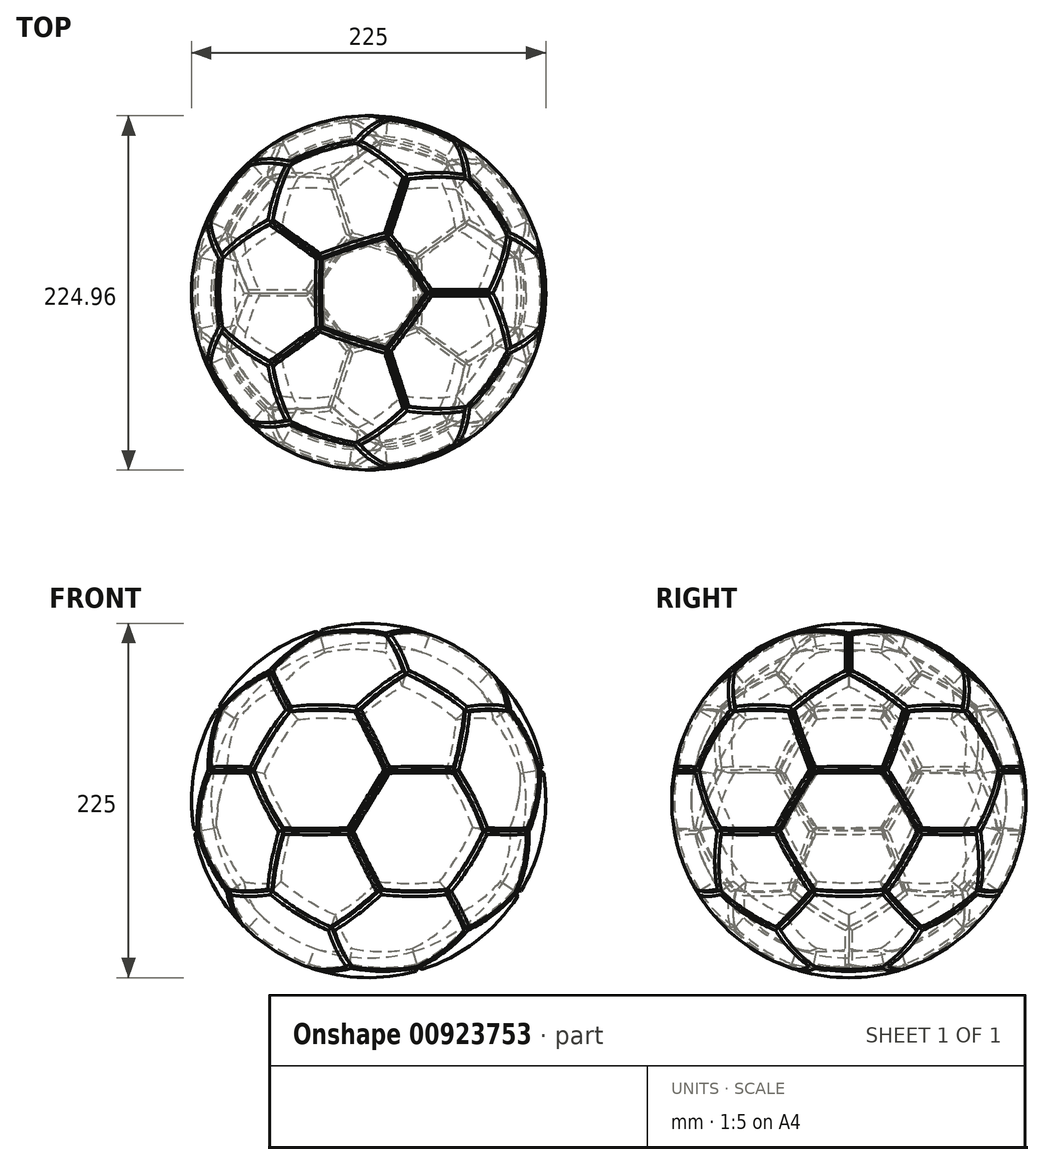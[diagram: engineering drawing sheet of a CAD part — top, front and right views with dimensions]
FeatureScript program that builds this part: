
annotation { "Feature Type Name" : "Feature", "Feature Type Description" : "" }
export const myFeature = defineFeature(function(context is Context, id is Id, definition is map)
    precondition{}
    {
        {
            var Q0;
            Q0=qCreatedBy(makeId("Top.planeOp"),FACE);
            var sketch = newSketch(context, id + "F0", { "sketchPlane" : qUnion([Q0])});
            skLineSegment(sketch, "E0.0", {"start": v(-13.14, 40.45) * mm, "end": v(34.4, 25) * mm});
            skLineSegment(sketch, "E0.1", {"start": v(34.4, 25) * mm, "end": v(34.4, -25) * mm});
            skLineSegment(sketch, "E0.2", {"start": v(34.4, -25) * mm, "end": v(-13.14, -40.45) * mm});
            skLineSegment(sketch, "E0.3", {"start": v(-13.14, -40.45) * mm, "end": v(-42.53, 0) * mm});
            skLineSegment(sketch, "E0.4", {"start": v(-42.53, 0) * mm, "end": v(-13.14, 40.45) * mm});
            skLineSegment(sketch, "E1", {"start": v(34.4, -25) * mm, "end": v(34.4, -50) * mm, "construction": true});
            skLineSegment(sketch, "E2", {"start": v(77.71, -50) * mm, "end": v(34.4, -50) * mm, "construction": true});
            skLineSegment(sketch, "E3", {"start": v(34.4, -25) * mm, "end": v(-27.84, 20.23) * mm, "construction": true});
            skLineSegment(sketch, "E4.MirrorCS", {"start": v(34.4, -25) * mm, "end": v(58.19, -17.27) * mm, "construction": true});
            skLineSegment(sketch, "E5.MirrorCS", {"start": v(71.57, -58.46) * mm, "end": v(58.19, -17.27) * mm, "construction": true});
            skSolve(sketch);
        }
        {
            var Q0;
            Q0=sQuery(id+"F0.wireOp",VERTEX,"E1.end");
            var Q1;
            Q1=sQuery(id+"F0.wireOp",EDGE,"E1");
            cPlane(context, id + "F1", {"entities" : qUnion([Q0, Q1]), "cplaneType" : CPlaneType.LINE_POINT, "offset" : 25 * mm, "width" : 150 * mm, "height" : 150 * mm});
        }
        {
            var Q0;
            Q0=qCreatedBy(id+"F1.planeOp",FACE);
            var sketch = newSketch(context, id + "F2", { "sketchPlane" : qUnion([Q0])});
            skCircle(sketch, "E6", {"center": v(34.4, 0) * mm, "radius": 43.3 * mm});
            skSolve(sketch);
        }
        {
            var Q0;
            Q0=sQuery(id+"F0.wireOp",VERTEX,"E4.MirrorCS.end");
            var Q1;
            Q1=sQuery(id+"F0.wireOp",EDGE,"E4.MirrorCS");
            cPlane(context, id + "F3", {"entities" : qUnion([Q0, Q1]), "cplaneType" : CPlaneType.LINE_POINT, "offset" : 25 * mm, "width" : 150 * mm, "height" : 150 * mm});
        }
        {
            var Q0;
            Q0=qCreatedBy(id+"F3.planeOp",FACE);
            var sketch = newSketch(context, id + "F4", { "sketchPlane" : qUnion([Q0])});
            skCircle(sketch, "E7", {"center": v(-34.4, 0) * mm, "radius": 43.3 * mm});
            skSolve(sketch);
        }
        {
            var Q0;
            Q0=makeQuery(id+"F2.imprint","IMPRINT",FACE,{"disambiguationData":[TD([[makeQuery(id+"F2.imprint","IMPRINT",EDGE,{"derivedFrom":sQuery(id+"F2.wireOp",EDGE,"E6")}),1.0]])]});
            extrude(context, id + "F5", {"entities" : qUnion([Q0]), "depth" : 25 * mm, "offsetDistance" : 25 * mm});
        }
        {
            var Q0;
            Q0=makeQuery(id+"F4.imprint","IMPRINT",FACE,{"disambiguationData":[TD([[makeQuery(id+"F4.imprint","IMPRINT",EDGE,{"derivedFrom":sQuery(id+"F4.wireOp",EDGE,"E7")}),1.0]])]});
            extrude(context, id + "F6", {"entities" : qUnion([Q0]), "depth" : 25 * mm, "offsetDistance" : 25 * mm});
        }
        {
            var Q0;
            Q0=makeQuery(id+"F5.opExtrude","SWEPT_BODY",BODY,{"disambiguationData":[OSD([sQuery(id+"F2.wireOp",EDGE,"E6")])]});
            var Q1;
            Q1=makeQuery(id+"F6.opExtrude","SWEPT_BODY",BODY,{"disambiguationData":[OSD([sQuery(id+"F4.wireOp",EDGE,"E7")])]});
            booleanBodies(context, id + "F7", {"operationType" : BooleanOperationType.INTERSECTION, "tools" : qUnion([Q0, Q1])});
        }
        {
            var Q0;
            Q0=sQuery(id+"F0.wireOp",VERTEX,"E0.0.end");
            var Q1;
            Q1=sQuery(id+"F0.wireOp",VERTEX,"E0.1.end");
            var Q2;
            {var subQ0=sQuery(id+"F4.wireOp",EDGE,"E7");var subQ1=sQuery(id+"F2.wireOp",EDGE,"E6");Q2=makeQuery(id+"F7.opBoolean","INTERSECT",VERTEX,{"disambiguationData":[OD(1.0)],"derivedFrom":[makeQuery(id+"F5.opExtrude","SWEPT_FACE",FACE,{"disambiguationData":[OSD([subQ1])]}),makeQuery(id+"F5.opExtrude","CAP_FACE",FACE,{"disambiguationData":[OSD([subQ1])],"isStart":true}),makeQuery(id+"F6.opExtrude","SWEPT_FACE",FACE,{"disambiguationData":[OSD([subQ0])]}),makeQuery(id+"F6.opExtrude","CAP_FACE",FACE,{"disambiguationData":[OSD([subQ0])],"isStart":true})]});}
            cPlane(context, id + "F8", {"entities" : qUnion([Q0, Q1, Q2]), "cplaneType" : CPlaneType.THREE_POINT, "offset" : 25 * mm, "width" : 150 * mm, "height" : 150 * mm});
        }
        {
            var Q0;
            Q0=qCreatedBy(id+"F8.planeOp",FACE);
            var sketch = newSketch(context, id + "F9", { "sketchPlane" : qUnion([Q0])});
            skLineSegment(sketch, "E8.0", {"start": v(113.95, 25) * mm, "end": v(113.95, -25) * mm});
            skLineSegment(sketch, "E8.1", {"start": v(113.95, -25) * mm, "end": v(70.64, -50) * mm});
            skLineSegment(sketch, "E8.2", {"start": v(70.64, -50) * mm, "end": v(27.34, -25) * mm});
            skLineSegment(sketch, "E8.3", {"start": v(27.34, -25) * mm, "end": v(27.34, 25) * mm});
            skLineSegment(sketch, "E8.4", {"start": v(27.34, 25) * mm, "end": v(70.64, 50) * mm});
            skLineSegment(sketch, "E8.5", {"start": v(70.64, 50) * mm, "end": v(113.95, 25) * mm});
            skLineSegment(sketch, "E9", {"start": v(70.64, 0) * mm, "end": v(27.34, -25) * mm, "construction": true});
            skSolve(sketch);
        }
        {
            var Q0;
            Q0=qCreatedBy(makeId("Front.planeOp"),FACE);
            var sketch = newSketch(context, id + "F10", { "sketchPlane" : qUnion([Q0])});
            skLineSegment(sketch, "E10", {"start": v(0, 0) * mm, "end": v(0, 116.37) * mm, "construction": true});
            skLineSegment(sketch, "E11", {"start": v(68.82, 26.29) * mm, "end": v(0, 116.37) * mm, "construction": true});
            skSolve(sketch);
        }
        {
            var Q0;
            Q0=makeQuery(id+"F0.imprint","IMPRINT",FACE,{"disambiguationData":[TD([[makeQuery(id+"F0.imprint","IMPRINT",EDGE,{"derivedFrom":sQuery(id+"F0.wireOp",EDGE,"E0.0")}),-1.0]])]});
            var Q1;
            Q1=sQuery(id+"F10.wireOp",VERTEX,"E10.end");
            loft(context, id + "F11", {"sheetProfilesArray" : [{ "sheetProfileEntities" : qUnion([Q0]) }, { "sheetProfileEntities" : qUnion([Q1]) }]});
        }
        {
            var Q1;
            Q1=makeQuery(id+"F9.imprint","IMPRINT",FACE,{"disambiguationData":[TD([[makeQuery(id+"F9.imprint","IMPRINT",EDGE,{"derivedFrom":sQuery(id+"F9.wireOp",EDGE,"E8.0")}),-1.0]])]});
            var Q2;
            Q2=sQuery(id+"F10.wireOp",VERTEX,"E10.end");
            loft(context, id + "F12", {"sheetProfilesArray" : [{ "sheetProfileEntities" : qUnion([Q1]) }, { "sheetProfileEntities" : qUnion([Q2]) }]});
        }
        {
            var Q0;
            Q0=makeQuery(id+"F12.opLoft","SWEPT_BODY",BODY,{"disambiguationData":[OSD([makeQuery(id+"F9.imprint","IMPRINT",FACE,{"disambiguationData":[TD([[makeQuery(id+"F9.imprint","IMPRINT",EDGE,{"derivedFrom":sQuery(id+"F9.wireOp",EDGE,"E8.0")}),-1.0]])]}),sQuery(id+"F10.wireOp",VERTEX,"E10.end")])]});
            var Q1;
            Q1=sQuery(id+"F10.wireOp",EDGE,"E10");
            circularPattern(context, id + "F13", {"entities" : qUnion([Q0]), "axis" : qUnion([Q1]), "angle" : 360 * degree, "instanceCount" : 5, "equalSpace" : true});
        }
        {
            var Q0;
            Q0=makeQuery(id+"F12.opLoft","MID_CAP_EDGE",EDGE,{"disambiguationData":[OSD([sQuery(id+"F9.wireOp",EDGE,"E8.3"),sQuery(id+"F9.wireOp",EDGE,"E8.4"),sQuery(id+"F9.wireOp",EDGE,"E8.5")])],"capPos":0.0});
            cPoint(context, id + "F14", {"entities" : qUnion([Q0]), "parameter" : 0.5});
        }
        {
            var Q0;
            Q0=sQuery(id+"F10.wireOp",VERTEX,"E11.start");
            var Q1;
            Q1=qCreatedBy(id+"F14",VERTEX);
            var Q2;
            Q2=sQuery(id+"F10.wireOp",VERTEX,"E10.end");
            cPlane(context, id + "F15", {"entities" : qUnion([Q0, Q1, Q2]), "cplaneType" : CPlaneType.THREE_POINT, "offset" : 25 * mm, "width" : 150 * mm, "height" : 150 * mm});
        }
        {
            var Q0;
            Q0=makeQuery(id+"F11.opLoft","SWEPT_BODY",BODY,{"disambiguationData":[OSD([makeQuery(id+"F0.imprint","IMPRINT",FACE,{"disambiguationData":[TD([[makeQuery(id+"F0.imprint","IMPRINT",EDGE,{"derivedFrom":sQuery(id+"F0.wireOp",EDGE,"E0.0")}),-1.0]])]}),sQuery(id+"F10.wireOp",VERTEX,"E10.end")])]});
            var Q1;
            Q1=qCreatedBy(id+"F15.planeOp",FACE);
            mirror(context, id + "F16", {"entities" : qUnion([Q0]), "mirrorPlane" : qUnion([Q1])});
        }
        {
            var Q0;
            Q0=makeQuery(id+"F16.opPattern","COPY",BODY,{"derivedFrom":makeQuery(id+"F11.opLoft","SWEPT_BODY",BODY,{"disambiguationData":[OSD([makeQuery(id+"F0.imprint","IMPRINT",FACE,{"disambiguationData":[TD([[makeQuery(id+"F0.imprint","IMPRINT",EDGE,{"derivedFrom":sQuery(id+"F0.wireOp",EDGE,"E0.0")}),-1.0]])]}),sQuery(id+"F10.wireOp",VERTEX,"E10.end")])]}),"instanceName":"1"});
            var Q1;
            Q1=sQuery(id+"F10.wireOp",EDGE,"E10");
            circularPattern(context, id + "F17", {"entities" : qUnion([Q0]), "axis" : qUnion([Q1]), "angle" : 360 * degree, "instanceCount" : 5, "equalSpace" : true});
        }
        {
            var Q0;
            Q0=makeQuery(id+"F12.opLoft","SWEPT_BODY",BODY,{"disambiguationData":[OSD([makeQuery(id+"F9.imprint","IMPRINT",FACE,{"disambiguationData":[TD([[makeQuery(id+"F9.imprint","IMPRINT",EDGE,{"derivedFrom":sQuery(id+"F9.wireOp",EDGE,"E8.0")}),-1.0]])]}),sQuery(id+"F10.wireOp",VERTEX,"E10.end")])]});
            var Q1;
            Q1=makeQuery(id+"F12.opLoft","SWEPT_FACE",FACE,{"disambiguationData":[OSD([sQuery(id+"F9.wireOp",EDGE,"E8.0"),sQuery(id+"F9.wireOp",EDGE,"E8.1"),sQuery(id+"F9.wireOp",EDGE,"E8.5")])]});
            mirror(context, id + "F18", {"entities" : qUnion([Q0]), "mirrorPlane" : qUnion([Q1])});
        }
        {
            var Q0;
            Q0=makeQuery(id+"F18.opPattern","COPY",BODY,{"derivedFrom":makeQuery(id+"F12.opLoft","SWEPT_BODY",BODY,{"disambiguationData":[OSD([makeQuery(id+"F9.imprint","IMPRINT",FACE,{"disambiguationData":[TD([[makeQuery(id+"F9.imprint","IMPRINT",EDGE,{"derivedFrom":sQuery(id+"F9.wireOp",EDGE,"E8.0")}),-1.0]])]}),sQuery(id+"F10.wireOp",VERTEX,"E10.end")])]}),"instanceName":"1"});
            var Q1;
            Q1=sQuery(id+"F10.wireOp",EDGE,"E10");
            circularPattern(context, id + "F19", {"entities" : qUnion([Q0]), "axis" : qUnion([Q1]), "angle" : 360 * degree, "instanceCount" : 5, "equalSpace" : true});
        }
        {
            var Q0;
            Q0=makeQuery(id+"F17.opPattern","COPY",EDGE,{"derivedFrom":makeQuery(id+"F16.opPattern","COPY",EDGE,{"derivedFrom":makeQuery(id+"F11.opLoft","MID_CAP_EDGE",EDGE,{"disambiguationData":[OSD([sQuery(id+"F0.wireOp",EDGE,"E0.0"),sQuery(id+"F0.wireOp",EDGE,"E0.3"),sQuery(id+"F0.wireOp",EDGE,"E0.4")])],"capPos":0.0}),"instanceName":"1"}),"instanceName":"1"});
            cPoint(context, id + "F20", {"entities" : qUnion([Q0]), "parameter" : 0.5});
        }
        {
            var Q0;
            Q0=makeQuery(id+"F19.opPattern","COPY",VERTEX,{"derivedFrom":makeQuery(id+"F18.opPattern","COPY",VERTEX,{"derivedFrom":makeQuery(id+"F12.opLoft","MID_CAP_VERTEX",VERTEX,{"disambiguationData":[OSD([sQuery(id+"F9.wireOp",EDGE,"E8.3"),sQuery(id+"F9.wireOp",EDGE,"E8.4")])],"capPos":0.0}),"instanceName":"1"}),"instanceName":"1"});
            var Q1;
            Q1=makeQuery(id+"F18.opPattern","COPY",VERTEX,{"derivedFrom":makeQuery(id+"F12.opLoft","MID_CAP_VERTEX",VERTEX,{"disambiguationData":[OSD([sQuery(id+"F9.wireOp",EDGE,"E8.2"),sQuery(id+"F9.wireOp",EDGE,"E8.3")])],"capPos":0.0}),"instanceName":"1"});
            var Q2;
            Q2=qCreatedBy(id+"F20",VERTEX);
            cPlane(context, id + "F21", {"entities" : qUnion([Q0, Q1, Q2]), "cplaneType" : CPlaneType.THREE_POINT, "offset" : 25 * mm, "width" : 150 * mm, "height" : 150 * mm});
        }
        {
            var Q0;
            Q0=qCreatedBy(id+"F21.planeOp",FACE);
            var sketch = newSketch(context, id + "F22", { "sketchPlane" : qUnion([Q0])});
            skLineSegment(sketch, "E12.0", {"start": v(34.36, 66.98) * mm, "end": v(-15.18, 73.73) * mm});
            skLineSegment(sketch, "E12.1", {"start": v(-15.18, 73.73) * mm, "end": v(-34.1, 120.01) * mm});
            skLineSegment(sketch, "E12.2", {"start": v(-34.1, 120.01) * mm, "end": v(-3.49, 159.54) * mm});
            skLineSegment(sketch, "E12.3", {"start": v(-3.49, 159.54) * mm, "end": v(46.06, 152.79) * mm});
            skLineSegment(sketch, "E12.4", {"start": v(46.06, 152.79) * mm, "end": v(64.98, 106.5) * mm});
            skLineSegment(sketch, "E12.5", {"start": v(64.98, 106.5) * mm, "end": v(34.36, 66.98) * mm});
            skSolve(sketch);
        }
        {
            var Q0;
            Q0=makeQuery(id+"F22.imprint","IMPRINT",FACE,{"disambiguationData":[TD([[makeQuery(id+"F22.imprint","IMPRINT",EDGE,{"derivedFrom":sQuery(id+"F22.wireOp",EDGE,"E12.0")}),-1.0]])]});
            var Q1;
            Q1=sQuery(id+"F10.wireOp",VERTEX,"E10.end");
            loft(context, id + "F23", {"sheetProfilesArray" : [{ "sheetProfileEntities" : qUnion([Q0]) }, { "sheetProfileEntities" : qUnion([Q1]) }]});
        }
        {
            var Q0;
            Q0=makeQuery(id+"F23.opLoft","SWEPT_BODY",BODY,{"disambiguationData":[OSD([sQuery(id+"F10.wireOp",VERTEX,"E10.end"),makeQuery(id+"F22.imprint","IMPRINT",FACE,{"disambiguationData":[TD([[makeQuery(id+"F22.imprint","IMPRINT",EDGE,{"derivedFrom":sQuery(id+"F22.wireOp",EDGE,"E12.0")}),-1.0]])]})])]});
            var Q1;
            Q1=sQuery(id+"F10.wireOp",EDGE,"E10");
            circularPattern(context, id + "F24", {"entities" : qUnion([Q0]), "axis" : qUnion([Q1]), "angle" : 360 * degree, "instanceCount" : 5, "equalSpace" : true});
        }
        {
            var Q0;
            Q0=makeQuery(id+"F19.opPattern","COPY",EDGE,{"derivedFrom":makeQuery(id+"F18.opPattern","COPY",EDGE,{"derivedFrom":makeQuery(id+"F12.opLoft","MID_CAP_EDGE",EDGE,{"disambiguationData":[OSD([sQuery(id+"F9.wireOp",EDGE,"E8.2"),sQuery(id+"F9.wireOp",EDGE,"E8.3"),sQuery(id+"F9.wireOp",EDGE,"E8.4")])],"capPos":0.0}),"instanceName":"1"}),"instanceName":"3"});
            cPoint(context, id + "F25", {"entities" : qUnion([Q0]), "parameter" : 0.5});
        }
        {
            var Q0;
            Q0=makeQuery(id+"F24.opPattern","COPY",VERTEX,{"derivedFrom":makeQuery(id+"F23.opLoft","MID_CAP_VERTEX",VERTEX,{"disambiguationData":[OSD([sQuery(id+"F22.wireOp",EDGE,"E12.2"),sQuery(id+"F22.wireOp",EDGE,"E12.3")])],"capPos":0.0}),"instanceName":"2"});
            var Q1;
            Q1=makeQuery(id+"F24.opPattern","COPY",VERTEX,{"derivedFrom":makeQuery(id+"F23.opLoft","MID_CAP_VERTEX",VERTEX,{"disambiguationData":[OSD([sQuery(id+"F22.wireOp",EDGE,"E12.3"),sQuery(id+"F22.wireOp",EDGE,"E12.4")])],"capPos":0.0}),"instanceName":"3"});
            var Q2;
            Q2=qCreatedBy(id+"F25",VERTEX);
            cPlane(context, id + "F26", {"entities" : qUnion([Q0, Q1, Q2]), "cplaneType" : CPlaneType.THREE_POINT, "offset" : 25 * mm, "width" : 150 * mm, "height" : 150 * mm});
        }
        {
            var Q0;
            Q0=qCreatedBy(id+"F26.planeOp",FACE);
            var sketch = newSketch(context, id + "F27", { "sketchPlane" : qUnion([Q0])});
            skLineSegment(sketch, "E13.0", {"start": v(2.25, 74) * mm, "end": v(-45.3, 58.54) * mm});
            skLineSegment(sketch, "E13.1", {"start": v(-45.3, 58.54) * mm, "end": v(-74.7, 99) * mm});
            skLineSegment(sketch, "E13.2", {"start": v(-74.7, 99) * mm, "end": v(-45.3, 139.44) * mm});
            skLineSegment(sketch, "E13.3", {"start": v(-45.3, 139.44) * mm, "end": v(2.25, 124) * mm});
            skLineSegment(sketch, "E13.4", {"start": v(2.25, 124) * mm, "end": v(2.25, 74) * mm});
            skSolve(sketch);
        }
        {
            var Q0;
            Q0=makeQuery(id+"F27.imprint","IMPRINT",FACE,{"disambiguationData":[TD([[makeQuery(id+"F27.imprint","IMPRINT",EDGE,{"derivedFrom":sQuery(id+"F27.wireOp",EDGE,"E13.0")}),-1.0]])]});
            var Q1;
            Q1=sQuery(id+"F10.wireOp",VERTEX,"E10.end");
            loft(context, id + "F28", {"sheetProfilesArray" : [{ "sheetProfileEntities" : qUnion([Q0]) }, { "sheetProfileEntities" : qUnion([Q1]) }]});
        }
        {
            var Q0;
            Q0=makeQuery(id+"F28.opLoft","SWEPT_BODY",BODY,{"disambiguationData":[OSD([sQuery(id+"F10.wireOp",VERTEX,"E10.end"),makeQuery(id+"F27.imprint","IMPRINT",FACE,{"disambiguationData":[TD([[makeQuery(id+"F27.imprint","IMPRINT",EDGE,{"derivedFrom":sQuery(id+"F27.wireOp",EDGE,"E13.0")}),-1.0]])]})])]});
            var Q1;
            Q1=sQuery(id+"F10.wireOp",EDGE,"E10");
            circularPattern(context, id + "F29", {"entities" : qUnion([Q0]), "axis" : qUnion([Q1]), "angle" : 360 * degree, "instanceCount" : 5, "equalSpace" : true});
        }
        {
            var Q0;
            Q0=makeQuery(id+"F23.opLoft","SWEPT_BODY",BODY,{"disambiguationData":[OSD([sQuery(id+"F10.wireOp",VERTEX,"E10.end"),makeQuery(id+"F22.imprint","IMPRINT",FACE,{"disambiguationData":[TD([[makeQuery(id+"F22.imprint","IMPRINT",EDGE,{"derivedFrom":sQuery(id+"F22.wireOp",EDGE,"E12.0")}),-1.0]])]})])]});
            var Q1;
            Q1=makeQuery(id+"F23.opLoft","SWEPT_FACE",FACE,{"disambiguationData":[OSD([sQuery(id+"F22.wireOp",EDGE,"E12.2"),sQuery(id+"F22.wireOp",EDGE,"E12.3"),sQuery(id+"F22.wireOp",EDGE,"E12.4")])]});
            mirror(context, id + "F30", {"entities" : qUnion([Q0]), "mirrorPlane" : qUnion([Q1])});
        }
        {
            var Q0;
            Q0=makeQuery(id+"F30.opPattern","COPY",BODY,{"derivedFrom":makeQuery(id+"F23.opLoft","SWEPT_BODY",BODY,{"disambiguationData":[OSD([sQuery(id+"F10.wireOp",VERTEX,"E10.end"),makeQuery(id+"F22.imprint","IMPRINT",FACE,{"disambiguationData":[TD([[makeQuery(id+"F22.imprint","IMPRINT",EDGE,{"derivedFrom":sQuery(id+"F22.wireOp",EDGE,"E12.0")}),-1.0]])]})])]}),"instanceName":"1"});
            var Q1;
            Q1=sQuery(id+"F10.wireOp",EDGE,"E10");
            circularPattern(context, id + "F31", {"entities" : qUnion([Q0]), "axis" : qUnion([Q1]), "angle" : 360 * degree, "instanceCount" : 5, "equalSpace" : true});
        }
        {
            var Q0;
            Q0=makeQuery(id+"F29.opPattern","COPY",EDGE,{"derivedFrom":makeQuery(id+"F28.opLoft","MID_CAP_EDGE",EDGE,{"disambiguationData":[OSD([sQuery(id+"F27.wireOp",EDGE,"E13.2"),sQuery(id+"F27.wireOp",EDGE,"E13.3"),sQuery(id+"F27.wireOp",EDGE,"E13.4")])],"capPos":0.0}),"instanceName":"4"});
            cPoint(context, id + "F32", {"entities" : qUnion([Q0]), "parameter" : 0.5});
        }
        {
            var Q0;
            Q0=makeQuery(id+"F31.opPattern","COPY",EDGE,{"derivedFrom":makeQuery(id+"F30.opPattern","COPY",EDGE,{"derivedFrom":makeQuery(id+"F23.opLoft","MID_CAP_EDGE",EDGE,{"disambiguationData":[OSD([sQuery(id+"F22.wireOp",EDGE,"E12.0"),sQuery(id+"F22.wireOp",EDGE,"E12.1"),sQuery(id+"F22.wireOp",EDGE,"E12.2")])],"capPos":0.0}),"instanceName":"1"}),"instanceName":"2"});
            cPoint(context, id + "F33", {"entities" : qUnion([Q0]), "parameter" : 0.5});
        }
        {
            var Q0;
            Q0=makeQuery(id+"F29.opPattern","COPY",EDGE,{"derivedFrom":makeQuery(id+"F28.opLoft","MID_CAP_EDGE",EDGE,{"disambiguationData":[OSD([sQuery(id+"F27.wireOp",EDGE,"E13.1"),sQuery(id+"F27.wireOp",EDGE,"E13.2"),sQuery(id+"F27.wireOp",EDGE,"E13.3")])],"capPos":0.0}),"instanceName":"1"});
            cPoint(context, id + "F34", {"entities" : qUnion([Q0]), "parameter" : 0.5});
        }
        {
            var Q0;
            Q0=qCreatedBy(id+"F32",VERTEX);
            var Q1;
            Q1=qCreatedBy(id+"F33",VERTEX);
            var Q2;
            Q2=qCreatedBy(id+"F34",VERTEX);
            cPlane(context, id + "F35", {"entities" : qUnion([Q0, Q1, Q2]), "cplaneType" : CPlaneType.THREE_POINT, "offset" : 25 * mm, "width" : 150 * mm, "height" : 150 * mm});
        }
        {
            var Q0;
            Q0=makeQuery(id+"F28.opLoft","SWEPT_BODY",BODY,{"disambiguationData":[OSD([sQuery(id+"F10.wireOp",VERTEX,"E10.end"),makeQuery(id+"F27.imprint","IMPRINT",FACE,{"disambiguationData":[TD([[makeQuery(id+"F27.imprint","IMPRINT",EDGE,{"derivedFrom":sQuery(id+"F27.wireOp",EDGE,"E13.0")}),-1.0]])]})])]});
            var Q1;
            Q1=qCreatedBy(id+"F35.planeOp",FACE);
            mirror(context, id + "F36", {"entities" : qUnion([Q0]), "mirrorPlane" : qUnion([Q1])});
        }
        {
            var Q0;
            Q0=makeQuery(id+"F7.opBoolean","INTERSECT",BODY,{"derivedFrom":[makeQuery(id+"F5.opExtrude","SWEPT_BODY",BODY,{"disambiguationData":[OSD([sQuery(id+"F2.wireOp",EDGE,"E6")])]}),makeQuery(id+"F6.opExtrude","SWEPT_BODY",BODY,{"disambiguationData":[OSD([sQuery(id+"F4.wireOp",EDGE,"E7")])]})]});
            deleteBodies(context, id + "F37", {"entities" : qUnion([Q0])});
        }
        {
            var Q0;
            Q0=sQuery(id+"F10.wireOp",EDGE,"E10");
            var Q1;
            Q1=sQuery(id+"F10.wireOp",VERTEX,"E10.end");
            cPlane(context, id + "F38", {"entities" : qUnion([Q0, Q1]), "cplaneType" : CPlaneType.LINE_POINT, "offset" : 25 * mm, "width" : 150 * mm, "height" : 150 * mm});
        }
        {
            var Q0;
            Q0=qCreatedBy(id+"F38.planeOp",FACE);
            var sketch = newSketch(context, id + "F39", { "sketchPlane" : qUnion([Q0])});
            skArc(sketch, "E14", {"start": v(100, 0) * mm, "mid": v(0, 100) * mm, "end": v(-100, 0) * mm});
            skLineSegment(sketch, "E15", {"start": v(100, 0) * mm, "end": v(-100, 0) * mm});
            skSolve(sketch);
        }
        {
            var Q0;
            Q0 = qSketchRegion(id + "F39", true);
            var Q1;
            Q1=sQuery(id+"F39.wireOp",EDGE,"E15");
            revolve(context, id + "F40", {"operationType" : NewBodyOperationType.REMOVE, "surfaceOperationType" : NewSurfaceOperationType.NEW, "entities" : qUnion([Q0]), "axis" : qUnion([Q1]), "revolveType" : RevolveType.FULL, "oppositeDirection" : true});
        }
        {
            var Q0;
            Q0=qCreatedBy(id+"F38.planeOp",FACE);
            var sketch = newSketch(context, id + "F41", { "sketchPlane" : qUnion([Q0])});
            skArc(sketch, "E16", {"start": v(112.5, 0) * mm, "mid": v(0, 112.5) * mm, "end": v(-112.5, 0) * mm});
            skLineSegment(sketch, "E17", {"start": v(112.5, 0) * mm, "end": v(125, 0) * mm});
            skArc(sketch, "E18", {"start": v(125, 0) * mm, "mid": v(0, 125) * mm, "end": v(-125, 0) * mm});
            skLineSegment(sketch, "E19.trimOffspring", {"start": v(-125, 0) * mm, "end": v(-112.5, 0) * mm});
            skSolve(sketch);
        }
        {
            var Q0;
            Q0=makeQuery(id+"F41.imprint","IMPRINT",FACE,{"disambiguationData":[TD([[makeQuery(id+"F41.imprint","IMPRINT",EDGE,{"derivedFrom":sQuery(id+"F41.wireOp",EDGE,"E16")}),-1.0]])]});
            var Q1;
            Q1=sQuery(id+"F41.wireOp",EDGE,"E17");
            revolve(context, id + "F42", {"operationType" : NewBodyOperationType.REMOVE, "surfaceOperationType" : NewSurfaceOperationType.NEW, "entities" : qUnion([Q0]), "axis" : qUnion([Q1]), "revolveType" : RevolveType.FULL, "oppositeDirection" : true});
        }
        {
            var Q0;
            {var subQ2=sQuery(id+"F22.wireOp",EDGE,"E12.1");var subQ3=sQuery(id+"F22.wireOp",EDGE,"E12.0");var subQ4=sQuery(id+"F22.wireOp",EDGE,"E12.5");Q0=makeQuery(id+"F42.boolean.opBoolean","COPY",FACE,{"disambiguationData":[TD([makeQuery(id+"F31.opPattern","COPY",FACE,{"derivedFrom":makeQuery(id+"F30.opPattern","COPY",FACE,{"derivedFrom":makeQuery(id+"F23.opLoft","SWEPT_FACE",FACE,{"disambiguationData":[OSD([subQ3,subQ2,subQ4])]}),"instanceName":"1"}),"instanceName":"3"})])],"derivedFrom":makeQuery(id+"F42.opRevolve","SWEPT_FACE",FACE,{"disambiguationData":[OSD([sQuery(id+"F41.wireOp",EDGE,"E16")])]})});}
            var Q1;
            {var subQ2=sQuery(id+"F22.wireOp",EDGE,"E12.1");var subQ3=sQuery(id+"F22.wireOp",EDGE,"E12.0");var subQ4=sQuery(id+"F22.wireOp",EDGE,"E12.5");Q1=makeQuery(id+"F42.boolean.opBoolean","COPY",FACE,{"disambiguationData":[TD([makeQuery(id+"F31.opPattern","COPY",FACE,{"derivedFrom":makeQuery(id+"F30.opPattern","COPY",FACE,{"derivedFrom":makeQuery(id+"F23.opLoft","SWEPT_FACE",FACE,{"disambiguationData":[OSD([subQ3,subQ2,subQ4])]}),"instanceName":"1"}),"instanceName":"4"})])],"derivedFrom":makeQuery(id+"F42.opRevolve","SWEPT_FACE",FACE,{"disambiguationData":[OSD([sQuery(id+"F41.wireOp",EDGE,"E16")])]})});}
            var Q2;
            {var subQ2=sQuery(id+"F27.wireOp",EDGE,"E13.1");var subQ3=sQuery(id+"F27.wireOp",EDGE,"E13.0");var subQ4=sQuery(id+"F27.wireOp",EDGE,"E13.4");Q2=makeQuery(id+"F42.boolean.opBoolean","COPY",FACE,{"disambiguationData":[TD([makeQuery(id+"F28.opLoft","SWEPT_FACE",FACE,{"disambiguationData":[OSD([subQ3,subQ2,subQ4])]})])],"derivedFrom":makeQuery(id+"F42.opRevolve","SWEPT_FACE",FACE,{"disambiguationData":[OSD([sQuery(id+"F41.wireOp",EDGE,"E16")])]})});}
            var Q3;
            {var subQ2=sQuery(id+"F22.wireOp",EDGE,"E12.1");var subQ3=sQuery(id+"F22.wireOp",EDGE,"E12.0");var subQ4=sQuery(id+"F22.wireOp",EDGE,"E12.5");Q3=makeQuery(id+"F42.boolean.opBoolean","COPY",FACE,{"disambiguationData":[TD([makeQuery(id+"F24.opPattern","COPY",FACE,{"derivedFrom":makeQuery(id+"F23.opLoft","SWEPT_FACE",FACE,{"disambiguationData":[OSD([subQ3,subQ2,subQ4])]}),"instanceName":"3"})])],"derivedFrom":makeQuery(id+"F42.opRevolve","SWEPT_FACE",FACE,{"disambiguationData":[OSD([sQuery(id+"F41.wireOp",EDGE,"E16")])]})});}
            var Q4;
            {var subQ2=sQuery(id+"F9.wireOp",EDGE,"E8.1");var subQ3=sQuery(id+"F9.wireOp",EDGE,"E8.0");var subQ4=sQuery(id+"F9.wireOp",EDGE,"E8.5");Q4=makeQuery(id+"F42.boolean.opBoolean","COPY",FACE,{"disambiguationData":[TD([makeQuery(id+"F19.opPattern","COPY",FACE,{"derivedFrom":makeQuery(id+"F18.opPattern","COPY",FACE,{"derivedFrom":makeQuery(id+"F12.opLoft","SWEPT_FACE",FACE,{"disambiguationData":[OSD([subQ3,subQ2,subQ4])]}),"instanceName":"1"}),"instanceName":"4"})])],"derivedFrom":makeQuery(id+"F42.opRevolve","SWEPT_FACE",FACE,{"disambiguationData":[OSD([sQuery(id+"F41.wireOp",EDGE,"E16")])]})});}
            var Q5;
            {var subQ2=sQuery(id+"F9.wireOp",EDGE,"E8.1");var subQ3=sQuery(id+"F9.wireOp",EDGE,"E8.0");var subQ4=sQuery(id+"F9.wireOp",EDGE,"E8.5");Q5=makeQuery(id+"F42.boolean.opBoolean","COPY",FACE,{"disambiguationData":[TD([makeQuery(id+"F19.opPattern","COPY",FACE,{"derivedFrom":makeQuery(id+"F18.opPattern","COPY",FACE,{"derivedFrom":makeQuery(id+"F12.opLoft","SWEPT_FACE",FACE,{"disambiguationData":[OSD([subQ3,subQ2,subQ4])]}),"instanceName":"1"}),"instanceName":"3"})])],"derivedFrom":makeQuery(id+"F42.opRevolve","SWEPT_FACE",FACE,{"disambiguationData":[OSD([sQuery(id+"F41.wireOp",EDGE,"E16")])]})});}
            var Q6;
            {var subQ2=sQuery(id+"F27.wireOp",EDGE,"E13.1");var subQ3=sQuery(id+"F27.wireOp",EDGE,"E13.0");var subQ4=sQuery(id+"F27.wireOp",EDGE,"E13.4");Q6=makeQuery(id+"F42.boolean.opBoolean","COPY",FACE,{"disambiguationData":[TD([makeQuery(id+"F29.opPattern","COPY",FACE,{"derivedFrom":makeQuery(id+"F28.opLoft","SWEPT_FACE",FACE,{"disambiguationData":[OSD([subQ3,subQ2,subQ4])]}),"instanceName":"1"})])],"derivedFrom":makeQuery(id+"F42.opRevolve","SWEPT_FACE",FACE,{"disambiguationData":[OSD([sQuery(id+"F41.wireOp",EDGE,"E16")])]})});}
            var Q7;
            {var subQ2=sQuery(id+"F22.wireOp",EDGE,"E12.1");var subQ3=sQuery(id+"F22.wireOp",EDGE,"E12.0");var subQ4=sQuery(id+"F22.wireOp",EDGE,"E12.5");Q7=makeQuery(id+"F42.boolean.opBoolean","COPY",FACE,{"disambiguationData":[TD([makeQuery(id+"F31.opPattern","COPY",FACE,{"derivedFrom":makeQuery(id+"F30.opPattern","COPY",FACE,{"derivedFrom":makeQuery(id+"F23.opLoft","SWEPT_FACE",FACE,{"disambiguationData":[OSD([subQ3,subQ2,subQ4])]}),"instanceName":"1"}),"instanceName":"2"})])],"derivedFrom":makeQuery(id+"F42.opRevolve","SWEPT_FACE",FACE,{"disambiguationData":[OSD([sQuery(id+"F41.wireOp",EDGE,"E16")])]})});}
            var Q8;
            {var subQ2=sQuery(id+"F27.wireOp",EDGE,"E13.1");var subQ3=sQuery(id+"F27.wireOp",EDGE,"E13.0");var subQ4=sQuery(id+"F27.wireOp",EDGE,"E13.4");Q8=makeQuery(id+"F42.boolean.opBoolean","COPY",FACE,{"disambiguationData":[TD([makeQuery(id+"F36.opPattern","COPY",FACE,{"derivedFrom":makeQuery(id+"F28.opLoft","SWEPT_FACE",FACE,{"disambiguationData":[OSD([subQ3,subQ2,subQ4])]}),"instanceName":"1"})])],"derivedFrom":makeQuery(id+"F42.opRevolve","SWEPT_FACE",FACE,{"disambiguationData":[OSD([sQuery(id+"F41.wireOp",EDGE,"E16")])]})});}
            var Q9;
            {var subQ2=sQuery(id+"F22.wireOp",EDGE,"E12.1");var subQ3=sQuery(id+"F22.wireOp",EDGE,"E12.0");var subQ4=sQuery(id+"F22.wireOp",EDGE,"E12.5");Q9=makeQuery(id+"F42.boolean.opBoolean","COPY",FACE,{"disambiguationData":[TD([makeQuery(id+"F24.opPattern","COPY",FACE,{"derivedFrom":makeQuery(id+"F23.opLoft","SWEPT_FACE",FACE,{"disambiguationData":[OSD([subQ3,subQ2,subQ4])]}),"instanceName":"2"})])],"derivedFrom":makeQuery(id+"F42.opRevolve","SWEPT_FACE",FACE,{"disambiguationData":[OSD([sQuery(id+"F41.wireOp",EDGE,"E16")])]})});}
            var Q10;
            {var subQ2=sQuery(id+"F27.wireOp",EDGE,"E13.1");var subQ3=sQuery(id+"F27.wireOp",EDGE,"E13.0");var subQ4=sQuery(id+"F27.wireOp",EDGE,"E13.4");Q10=makeQuery(id+"F42.boolean.opBoolean","COPY",FACE,{"disambiguationData":[TD([makeQuery(id+"F29.opPattern","COPY",FACE,{"derivedFrom":makeQuery(id+"F28.opLoft","SWEPT_FACE",FACE,{"disambiguationData":[OSD([subQ3,subQ2,subQ4])]}),"instanceName":"4"})])],"derivedFrom":makeQuery(id+"F42.opRevolve","SWEPT_FACE",FACE,{"disambiguationData":[OSD([sQuery(id+"F41.wireOp",EDGE,"E16")])]})});}
            var Q11;
            {var subQ2=sQuery(id+"F9.wireOp",EDGE,"E8.1");var subQ3=sQuery(id+"F9.wireOp",EDGE,"E8.0");var subQ4=sQuery(id+"F9.wireOp",EDGE,"E8.5");Q11=makeQuery(id+"F42.boolean.opBoolean","COPY",FACE,{"disambiguationData":[TD([makeQuery(id+"F19.opPattern","COPY",FACE,{"derivedFrom":makeQuery(id+"F18.opPattern","COPY",FACE,{"derivedFrom":makeQuery(id+"F12.opLoft","SWEPT_FACE",FACE,{"disambiguationData":[OSD([subQ3,subQ2,subQ4])]}),"instanceName":"1"}),"instanceName":"2"})])],"derivedFrom":makeQuery(id+"F42.opRevolve","SWEPT_FACE",FACE,{"disambiguationData":[OSD([sQuery(id+"F41.wireOp",EDGE,"E16")])]})});}
            var Q12;
            {var subQ2=sQuery(id+"F0.wireOp",EDGE,"E0.1");var subQ3=sQuery(id+"F0.wireOp",EDGE,"E0.0");var subQ4=sQuery(id+"F0.wireOp",EDGE,"E0.4");Q12=makeQuery(id+"F42.boolean.opBoolean","COPY",FACE,{"disambiguationData":[TD([makeQuery(id+"F17.opPattern","COPY",FACE,{"derivedFrom":makeQuery(id+"F16.opPattern","COPY",FACE,{"derivedFrom":makeQuery(id+"F11.opLoft","SWEPT_FACE",FACE,{"disambiguationData":[OSD([subQ3,subQ2,subQ4])]}),"instanceName":"1"}),"instanceName":"3"})])],"derivedFrom":makeQuery(id+"F42.opRevolve","SWEPT_FACE",FACE,{"disambiguationData":[OSD([sQuery(id+"F41.wireOp",EDGE,"E16")])]})});}
            var Q13;
            {var subQ2=sQuery(id+"F9.wireOp",EDGE,"E8.1");var subQ3=sQuery(id+"F9.wireOp",EDGE,"E8.0");var subQ4=sQuery(id+"F9.wireOp",EDGE,"E8.5");Q13=makeQuery(id+"F42.boolean.opBoolean","COPY",FACE,{"disambiguationData":[TD([makeQuery(id+"F13.opPattern","COPY",FACE,{"derivedFrom":makeQuery(id+"F12.opLoft","SWEPT_FACE",FACE,{"disambiguationData":[OSD([subQ3,subQ2,subQ4])]}),"instanceName":"3"})])],"derivedFrom":makeQuery(id+"F42.opRevolve","SWEPT_FACE",FACE,{"disambiguationData":[OSD([sQuery(id+"F41.wireOp",EDGE,"E16")])]})});}
            var Q14;
            {var subQ2=sQuery(id+"F9.wireOp",EDGE,"E8.1");var subQ3=sQuery(id+"F9.wireOp",EDGE,"E8.0");var subQ4=sQuery(id+"F9.wireOp",EDGE,"E8.5");Q14=makeQuery(id+"F42.boolean.opBoolean","COPY",FACE,{"disambiguationData":[TD([makeQuery(id+"F13.opPattern","COPY",FACE,{"derivedFrom":makeQuery(id+"F12.opLoft","SWEPT_FACE",FACE,{"disambiguationData":[OSD([subQ3,subQ2,subQ4])]}),"instanceName":"2"})])],"derivedFrom":makeQuery(id+"F42.opRevolve","SWEPT_FACE",FACE,{"disambiguationData":[OSD([sQuery(id+"F41.wireOp",EDGE,"E16")])]})});}
            var Q15;
            {var subQ2=sQuery(id+"F0.wireOp",EDGE,"E0.1");var subQ3=sQuery(id+"F0.wireOp",EDGE,"E0.0");var subQ4=sQuery(id+"F0.wireOp",EDGE,"E0.4");Q15=makeQuery(id+"F42.boolean.opBoolean","COPY",FACE,{"disambiguationData":[TD([makeQuery(id+"F11.opLoft","SWEPT_FACE",FACE,{"disambiguationData":[OSD([subQ3,subQ2,subQ4])]})])],"derivedFrom":makeQuery(id+"F42.opRevolve","SWEPT_FACE",FACE,{"disambiguationData":[OSD([sQuery(id+"F41.wireOp",EDGE,"E16")])]})});}
            var Q16;
            {var subQ2=sQuery(id+"F9.wireOp",EDGE,"E8.1");var subQ3=sQuery(id+"F9.wireOp",EDGE,"E8.0");var subQ4=sQuery(id+"F9.wireOp",EDGE,"E8.5");Q16=makeQuery(id+"F42.boolean.opBoolean","COPY",FACE,{"disambiguationData":[TD([makeQuery(id+"F13.opPattern","COPY",FACE,{"derivedFrom":makeQuery(id+"F12.opLoft","SWEPT_FACE",FACE,{"disambiguationData":[OSD([subQ3,subQ2,subQ4])]}),"instanceName":"4"})])],"derivedFrom":makeQuery(id+"F42.opRevolve","SWEPT_FACE",FACE,{"disambiguationData":[OSD([sQuery(id+"F41.wireOp",EDGE,"E16")])]})});}
            var Q17;
            {var subQ2=sQuery(id+"F9.wireOp",EDGE,"E8.1");var subQ3=sQuery(id+"F9.wireOp",EDGE,"E8.0");var subQ4=sQuery(id+"F9.wireOp",EDGE,"E8.5");Q17=makeQuery(id+"F42.boolean.opBoolean","COPY",FACE,{"disambiguationData":[TD([makeQuery(id+"F12.opLoft","SWEPT_FACE",FACE,{"disambiguationData":[OSD([subQ3,subQ2,subQ4])]})])],"derivedFrom":makeQuery(id+"F42.opRevolve","SWEPT_FACE",FACE,{"disambiguationData":[OSD([sQuery(id+"F41.wireOp",EDGE,"E16")])]})});}
            var Q18;
            {var subQ2=sQuery(id+"F9.wireOp",EDGE,"E8.1");var subQ3=sQuery(id+"F9.wireOp",EDGE,"E8.0");var subQ4=sQuery(id+"F9.wireOp",EDGE,"E8.5");Q18=makeQuery(id+"F42.boolean.opBoolean","COPY",FACE,{"disambiguationData":[TD([makeQuery(id+"F13.opPattern","COPY",FACE,{"derivedFrom":makeQuery(id+"F12.opLoft","SWEPT_FACE",FACE,{"disambiguationData":[OSD([subQ3,subQ2,subQ4])]}),"instanceName":"1"})])],"derivedFrom":makeQuery(id+"F42.opRevolve","SWEPT_FACE",FACE,{"disambiguationData":[OSD([sQuery(id+"F41.wireOp",EDGE,"E16")])]})});}
            var Q19;
            {var subQ2=sQuery(id+"F9.wireOp",EDGE,"E8.1");var subQ3=sQuery(id+"F9.wireOp",EDGE,"E8.0");var subQ4=sQuery(id+"F9.wireOp",EDGE,"E8.5");Q19=makeQuery(id+"F42.boolean.opBoolean","COPY",FACE,{"disambiguationData":[TD([makeQuery(id+"F19.opPattern","COPY",FACE,{"derivedFrom":makeQuery(id+"F18.opPattern","COPY",FACE,{"derivedFrom":makeQuery(id+"F12.opLoft","SWEPT_FACE",FACE,{"disambiguationData":[OSD([subQ3,subQ2,subQ4])]}),"instanceName":"1"}),"instanceName":"1"})])],"derivedFrom":makeQuery(id+"F42.opRevolve","SWEPT_FACE",FACE,{"disambiguationData":[OSD([sQuery(id+"F41.wireOp",EDGE,"E16")])]})});}
            var Q20;
            {var subQ2=sQuery(id+"F22.wireOp",EDGE,"E12.1");var subQ3=sQuery(id+"F22.wireOp",EDGE,"E12.0");var subQ4=sQuery(id+"F22.wireOp",EDGE,"E12.5");Q20=makeQuery(id+"F42.boolean.opBoolean","COPY",FACE,{"disambiguationData":[TD([makeQuery(id+"F30.opPattern","COPY",FACE,{"derivedFrom":makeQuery(id+"F23.opLoft","SWEPT_FACE",FACE,{"disambiguationData":[OSD([subQ3,subQ2,subQ4])]}),"instanceName":"1"})])],"derivedFrom":makeQuery(id+"F42.opRevolve","SWEPT_FACE",FACE,{"disambiguationData":[OSD([sQuery(id+"F41.wireOp",EDGE,"E16")])]})});}
            var Q21;
            {var subQ2=sQuery(id+"F22.wireOp",EDGE,"E12.1");var subQ3=sQuery(id+"F22.wireOp",EDGE,"E12.0");var subQ4=sQuery(id+"F22.wireOp",EDGE,"E12.5");Q21=makeQuery(id+"F42.boolean.opBoolean","COPY",FACE,{"disambiguationData":[TD([makeQuery(id+"F31.opPattern","COPY",FACE,{"derivedFrom":makeQuery(id+"F30.opPattern","COPY",FACE,{"derivedFrom":makeQuery(id+"F23.opLoft","SWEPT_FACE",FACE,{"disambiguationData":[OSD([subQ3,subQ2,subQ4])]}),"instanceName":"1"}),"instanceName":"1"})])],"derivedFrom":makeQuery(id+"F42.opRevolve","SWEPT_FACE",FACE,{"disambiguationData":[OSD([sQuery(id+"F41.wireOp",EDGE,"E16")])]})});}
            var Q22;
            {var subQ2=sQuery(id+"F22.wireOp",EDGE,"E12.1");var subQ3=sQuery(id+"F22.wireOp",EDGE,"E12.0");var subQ4=sQuery(id+"F22.wireOp",EDGE,"E12.5");Q22=makeQuery(id+"F42.boolean.opBoolean","COPY",FACE,{"disambiguationData":[TD([makeQuery(id+"F24.opPattern","COPY",FACE,{"derivedFrom":makeQuery(id+"F23.opLoft","SWEPT_FACE",FACE,{"disambiguationData":[OSD([subQ3,subQ2,subQ4])]}),"instanceName":"1"})])],"derivedFrom":makeQuery(id+"F42.opRevolve","SWEPT_FACE",FACE,{"disambiguationData":[OSD([sQuery(id+"F41.wireOp",EDGE,"E16")])]})});}
            var Q23;
            {var subQ2=sQuery(id+"F27.wireOp",EDGE,"E13.1");var subQ3=sQuery(id+"F27.wireOp",EDGE,"E13.0");var subQ4=sQuery(id+"F27.wireOp",EDGE,"E13.4");Q23=makeQuery(id+"F42.boolean.opBoolean","COPY",FACE,{"disambiguationData":[TD([makeQuery(id+"F29.opPattern","COPY",FACE,{"derivedFrom":makeQuery(id+"F28.opLoft","SWEPT_FACE",FACE,{"disambiguationData":[OSD([subQ3,subQ2,subQ4])]}),"instanceName":"3"})])],"derivedFrom":makeQuery(id+"F42.opRevolve","SWEPT_FACE",FACE,{"disambiguationData":[OSD([sQuery(id+"F41.wireOp",EDGE,"E16")])]})});}
            var Q24;
            {var subQ2=sQuery(id+"F22.wireOp",EDGE,"E12.1");var subQ3=sQuery(id+"F22.wireOp",EDGE,"E12.0");var subQ4=sQuery(id+"F22.wireOp",EDGE,"E12.5");Q24=makeQuery(id+"F42.boolean.opBoolean","COPY",FACE,{"disambiguationData":[TD([makeQuery(id+"F23.opLoft","SWEPT_FACE",FACE,{"disambiguationData":[OSD([subQ3,subQ2,subQ4])]})])],"derivedFrom":makeQuery(id+"F42.opRevolve","SWEPT_FACE",FACE,{"disambiguationData":[OSD([sQuery(id+"F41.wireOp",EDGE,"E16")])]})});}
            var Q25;
            {var subQ2=sQuery(id+"F9.wireOp",EDGE,"E8.1");var subQ3=sQuery(id+"F9.wireOp",EDGE,"E8.0");var subQ4=sQuery(id+"F9.wireOp",EDGE,"E8.5");Q25=makeQuery(id+"F42.boolean.opBoolean","COPY",FACE,{"disambiguationData":[TD([makeQuery(id+"F18.opPattern","COPY",FACE,{"derivedFrom":makeQuery(id+"F12.opLoft","SWEPT_FACE",FACE,{"disambiguationData":[OSD([subQ3,subQ2,subQ4])]}),"instanceName":"1"})])],"derivedFrom":makeQuery(id+"F42.opRevolve","SWEPT_FACE",FACE,{"disambiguationData":[OSD([sQuery(id+"F41.wireOp",EDGE,"E16")])]})});}
            var Q26;
            {var subQ2=sQuery(id+"F22.wireOp",EDGE,"E12.1");var subQ3=sQuery(id+"F22.wireOp",EDGE,"E12.0");var subQ4=sQuery(id+"F22.wireOp",EDGE,"E12.5");Q26=makeQuery(id+"F42.boolean.opBoolean","COPY",FACE,{"disambiguationData":[TD([makeQuery(id+"F24.opPattern","COPY",FACE,{"derivedFrom":makeQuery(id+"F23.opLoft","SWEPT_FACE",FACE,{"disambiguationData":[OSD([subQ3,subQ2,subQ4])]}),"instanceName":"4"})])],"derivedFrom":makeQuery(id+"F42.opRevolve","SWEPT_FACE",FACE,{"disambiguationData":[OSD([sQuery(id+"F41.wireOp",EDGE,"E16")])]})});}
            var Q27;
            {var subQ2=sQuery(id+"F27.wireOp",EDGE,"E13.1");var subQ3=sQuery(id+"F27.wireOp",EDGE,"E13.0");var subQ4=sQuery(id+"F27.wireOp",EDGE,"E13.4");Q27=makeQuery(id+"F42.boolean.opBoolean","COPY",FACE,{"disambiguationData":[TD([makeQuery(id+"F29.opPattern","COPY",FACE,{"derivedFrom":makeQuery(id+"F28.opLoft","SWEPT_FACE",FACE,{"disambiguationData":[OSD([subQ3,subQ2,subQ4])]}),"instanceName":"2"})])],"derivedFrom":makeQuery(id+"F42.opRevolve","SWEPT_FACE",FACE,{"disambiguationData":[OSD([sQuery(id+"F41.wireOp",EDGE,"E16")])]})});}
            var Q28;
            {var subQ2=sQuery(id+"F0.wireOp",EDGE,"E0.1");var subQ3=sQuery(id+"F0.wireOp",EDGE,"E0.0");var subQ4=sQuery(id+"F0.wireOp",EDGE,"E0.4");Q28=makeQuery(id+"F42.boolean.opBoolean","COPY",FACE,{"disambiguationData":[TD([makeQuery(id+"F17.opPattern","COPY",FACE,{"derivedFrom":makeQuery(id+"F16.opPattern","COPY",FACE,{"derivedFrom":makeQuery(id+"F11.opLoft","SWEPT_FACE",FACE,{"disambiguationData":[OSD([subQ3,subQ2,subQ4])]}),"instanceName":"1"}),"instanceName":"1"})])],"derivedFrom":makeQuery(id+"F42.opRevolve","SWEPT_FACE",FACE,{"disambiguationData":[OSD([sQuery(id+"F41.wireOp",EDGE,"E16")])]})});}
            var Q29;
            {var subQ2=sQuery(id+"F0.wireOp",EDGE,"E0.1");var subQ3=sQuery(id+"F0.wireOp",EDGE,"E0.0");var subQ4=sQuery(id+"F0.wireOp",EDGE,"E0.4");Q29=makeQuery(id+"F42.boolean.opBoolean","COPY",FACE,{"disambiguationData":[TD([makeQuery(id+"F17.opPattern","COPY",FACE,{"derivedFrom":makeQuery(id+"F16.opPattern","COPY",FACE,{"derivedFrom":makeQuery(id+"F11.opLoft","SWEPT_FACE",FACE,{"disambiguationData":[OSD([subQ3,subQ2,subQ4])]}),"instanceName":"1"}),"instanceName":"2"})])],"derivedFrom":makeQuery(id+"F42.opRevolve","SWEPT_FACE",FACE,{"disambiguationData":[OSD([sQuery(id+"F41.wireOp",EDGE,"E16")])]})});}
            var Q30;
            {var subQ2=sQuery(id+"F0.wireOp",EDGE,"E0.1");var subQ3=sQuery(id+"F0.wireOp",EDGE,"E0.0");var subQ4=sQuery(id+"F0.wireOp",EDGE,"E0.4");Q30=makeQuery(id+"F42.boolean.opBoolean","COPY",FACE,{"disambiguationData":[TD([makeQuery(id+"F16.opPattern","COPY",FACE,{"derivedFrom":makeQuery(id+"F11.opLoft","SWEPT_FACE",FACE,{"disambiguationData":[OSD([subQ3,subQ2,subQ4])]}),"instanceName":"1"})])],"derivedFrom":makeQuery(id+"F42.opRevolve","SWEPT_FACE",FACE,{"disambiguationData":[OSD([sQuery(id+"F41.wireOp",EDGE,"E16")])]})});}
            var Q31;
            {var subQ2=sQuery(id+"F0.wireOp",EDGE,"E0.1");var subQ3=sQuery(id+"F0.wireOp",EDGE,"E0.0");var subQ4=sQuery(id+"F0.wireOp",EDGE,"E0.4");Q31=makeQuery(id+"F42.boolean.opBoolean","COPY",FACE,{"disambiguationData":[TD([makeQuery(id+"F17.opPattern","COPY",FACE,{"derivedFrom":makeQuery(id+"F16.opPattern","COPY",FACE,{"derivedFrom":makeQuery(id+"F11.opLoft","SWEPT_FACE",FACE,{"disambiguationData":[OSD([subQ3,subQ2,subQ4])]}),"instanceName":"1"}),"instanceName":"4"})])],"derivedFrom":makeQuery(id+"F42.opRevolve","SWEPT_FACE",FACE,{"disambiguationData":[OSD([sQuery(id+"F41.wireOp",EDGE,"E16")])]})});}
            chamfer(context, id + "F43", {"entities" : qUnion([Q0, Q1, Q2, Q3, Q4, Q5, Q6, Q7, Q8, Q9, Q10, Q11, Q12, Q13, Q14, Q15, Q16, Q17, Q18, Q19, Q20, Q21, Q22, Q23, Q24, Q25, Q26, Q27, Q28, Q29, Q30, Q31]), "width" : 2 * mm, "tangentPropagation" : true});
        }
    });
